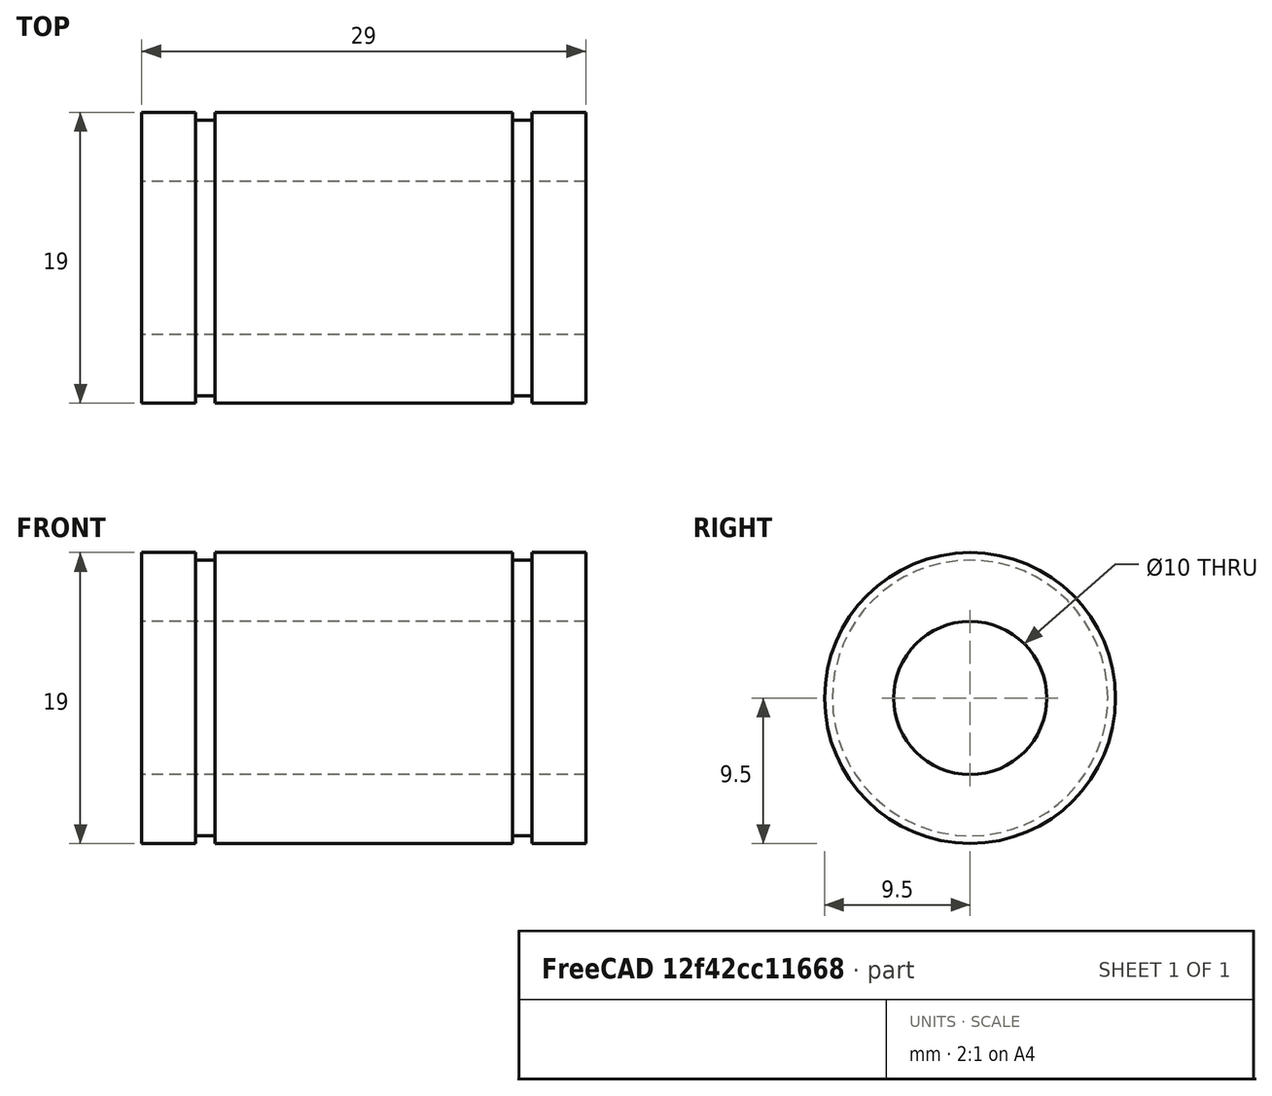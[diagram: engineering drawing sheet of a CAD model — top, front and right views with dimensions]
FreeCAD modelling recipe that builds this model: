
FCSTD DOCUMENT
Label: LM10UU_LinearBearing
objects: Sketcher::SketchObject×1, PartDesign::Revolution×1
note: 3 computed .brp shape members not serialized (recipe doc carries the construction recipe); baked Part::Feature solids carry a one-line shape summary decoded from their .brp

FEATURE [Sketcher::SketchObject] Sketch
  Placement = pos=(0,0,0) rot=(1,0,0;1.5708rad)
  sketch-geometry (12):
    g0: LineSegment StartX=-14.5 StartY=9.5 StartZ=0 EndX=-11 EndY=9.5 EndZ=0
    g1: LineSegment StartX=14.5 StartY=9.5 StartZ=0 EndX=14.5 EndY=5 EndZ=0
    g2: LineSegment StartX=14.5 StartY=5 StartZ=0 EndX=-14.5 EndY=5 EndZ=0
    g3: LineSegment StartX=-14.5 StartY=5 StartZ=0 EndX=-14.5 EndY=9.5 EndZ=0
    g4: LineSegment StartX=-9.7 StartY=9.5 StartZ=0 EndX=-9.7 EndY=9 EndZ=0
    g5: LineSegment StartX=-9.7 StartY=9 StartZ=0 EndX=-11 EndY=9 EndZ=0
    g6: LineSegment StartX=-11 StartY=9 StartZ=0 EndX=-11 EndY=9.5 EndZ=0
    g7: LineSegment StartX=11 StartY=9.5 StartZ=0 EndX=11 EndY=9 EndZ=0
    g8: LineSegment StartX=11 StartY=9 StartZ=0 EndX=9.7 EndY=9 EndZ=0
    g9: LineSegment StartX=9.7 StartY=9 StartZ=0 EndX=9.7 EndY=9.5 EndZ=0
    g10: LineSegment StartX=11 StartY=9.5 StartZ=0 EndX=14.5 EndY=9.5 EndZ=0
    g11: LineSegment StartX=-9.7 StartY=9.5 StartZ=0 EndX=9.7 EndY=9.5 EndZ=0
  constraints (34):
    c: Coincident(g10,g1)
    c: Coincident(g1,g2)
    c: Coincident(g2,g3)
    c: Coincident(g3,g0)
    c: Horizontal(g0)
    c: Horizontal(g2)
    c: Vertical(g1)
    c: Vertical(g3)
    c: Coincident(g4,g5)
    c: Coincident(g5,g6)
    c: Horizontal(g5)
    c: Vertical(g4)
    c: Vertical(g6)
    c: Coincident(g7,g8)
    c: Coincident(g8,g9)
    c: Horizontal(g8)
    c: Vertical(g7)
    c: Vertical(g9)
    c: Coincident(g11,g9)
    c: Coincident(g10,g7)
    c: Tangent(g0,g10)
    c: Coincident(g0,g6)
    c: Coincident(g11,g4)
    c: Tangent(g0,g11)
    c: Equal(g4,g9)
    c: Equal(g5,g8)
    c: Equal(g0,g10)
    c: DistanceX(g8) = -1.3
    c: DistanceX(g0,g7) = 22
    c: DistanceX(g2) = -29
    c: DistanceY(g2) = 5
    c: DistanceY(g5) = 9
    c: DistanceY(g0) = 9.5
    c: Symmetric(g0,g1,g-2)
FEATURE [PartDesign::Revolution] Revolution
  Angle = 360
  Axis = (1,0,0)
  Base = (0,0,0)
  Placement = pos=(0,0,0) rot=(1,0,0;1.5708rad)
  ReferenceAxis = -> Sketch [H_Axis]
  Sketch = -> Sketch
